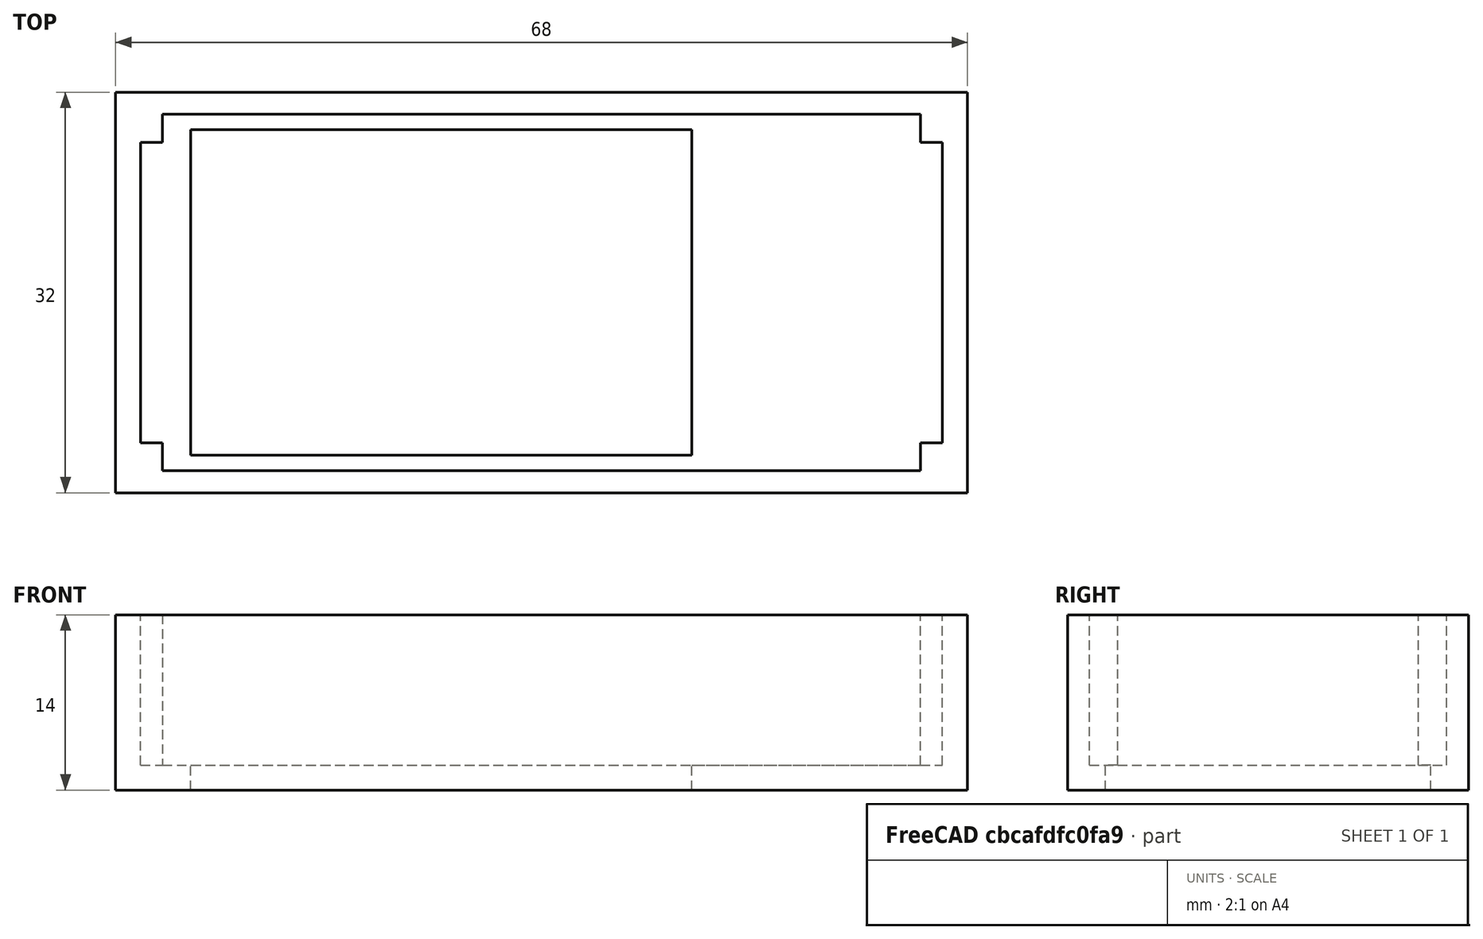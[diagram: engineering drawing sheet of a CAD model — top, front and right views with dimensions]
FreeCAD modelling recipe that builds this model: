
FCSTD DOCUMENT  (FreeCAD 0.15R4671 (Git))
Label: cap_top
License: All rights reserved
LicenseURL: http://en.wikipedia.org/wiki/All_rights_reserved
objects: Part::Box×4, Part::MultiFuse×1, Part::Cut×1, Mesh::Feature×1
note: 6 computed .brp shape members not serialized (recipe doc carries the construction recipe); baked Part::Feature solids carry a one-line shape summary decoded from their .brp

FEATURE [Part::Box] Box  label="Cube"
  Height = 14
  Length = 68
  Width = 32
FEATURE [Part::Box] Box001  label="Cube001"
  Height = 12
  Length = 60.5
  Placement = pos=(3.75,1.75,2) rot=(0,0,1;0rad)
  Width = 28.5
FEATURE [Part::Box] Box002  label="Cube002"
  Height = 12
  Length = 64
  Placement = pos=(2,4,2) rot=(0,0,1;0rad)
  Width = 24
FEATURE [Part::Box] Box003  label="Cube003"
  Height = 18
  Length = 40
  Placement = pos=(6,3,0) rot=(0,0,1;0rad)
  Width = 26
FEATURE [Part::MultiFuse] Fusion
  Shapes = -> [Box003,Box002,Box001]
FEATURE [Part::Cut] Cut
  Base = -> Box
  Tool = -> Fusion
FEATURE [Mesh::Feature] Mesh  label="Cut (Meshed)"
